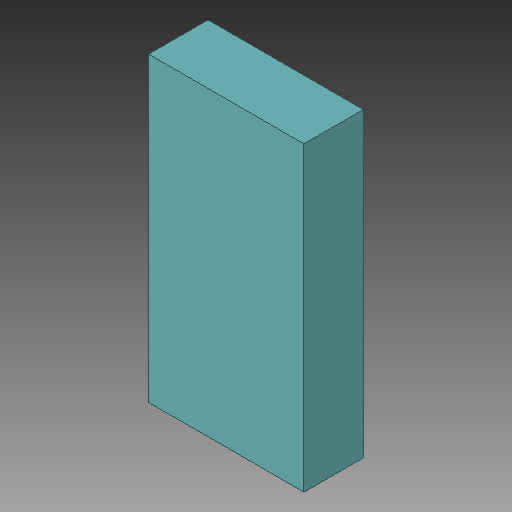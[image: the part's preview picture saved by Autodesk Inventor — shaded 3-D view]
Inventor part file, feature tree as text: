
AUTODESK INVENTOR PART (.ipt)
format: ipt  version: 2018 (Build 220112000, 112)  size: 79,872 bytes
history: native  units: in
note: dims shown in document units (in); Inventor stores cm internally (conversion verified against a paired STEP export)
features: other x1, extrude x1
ambient origin geometry x8: Origin, YZ Plane, XZ Plane, XY Plane, X Axis, Y Axis, Z Axis, Center Point
bodies: Solid1 (feature_tree)
feature tree (2):
  other  "JP1M, RXD_73"
  extrude  "Extrusion1"  Depth=0.0394in TaperAngle=0.0deg
